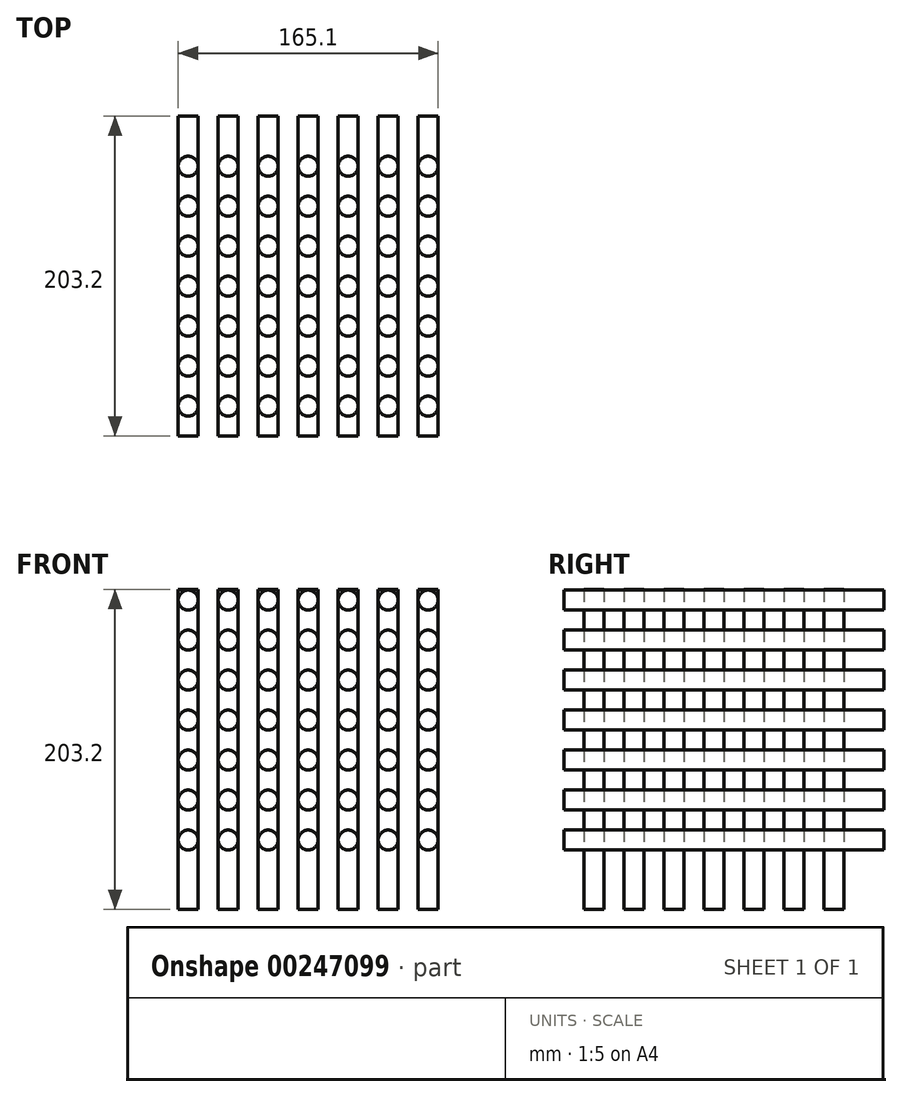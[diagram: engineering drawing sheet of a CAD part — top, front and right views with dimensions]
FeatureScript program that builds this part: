
annotation { "Feature Type Name" : "Feature", "Feature Type Description" : "" }
export const myFeature = defineFeature(function(context is Context, id is Id, definition is map)
    precondition{}
    {
        {
            var Q0;
            Q0=qCreatedBy(makeId("Front.planeOp"),FACE);
            var sketch = newSketch(context, id + "F0", { "sketchPlane" : qUnion([Q0])});
            skCircle(sketch, "E0", {"center": v(-69.84, -57.55) * mm, "radius": 6.35 * mm});
            skCircle(sketch, "E1.0.1.0", {"center": v(-69.84, -32.15) * mm, "radius": 6.35 * mm});
            skCircle(sketch, "E1.0.2.0", {"center": v(-69.84, -6.75) * mm, "radius": 6.35 * mm});
            skCircle(sketch, "E1.0.3.0", {"center": v(-69.84, 18.65) * mm, "radius": 6.35 * mm});
            skCircle(sketch, "E1.0.4.0", {"center": v(-69.84, 44.05) * mm, "radius": 6.35 * mm});
            skCircle(sketch, "E1.0.5.0", {"center": v(-69.84, 69.45) * mm, "radius": 6.35 * mm});
            skCircle(sketch, "E1.0.6.0", {"center": v(-69.84, 94.85) * mm, "radius": 6.35 * mm});
            skCircle(sketch, "E1.1.0.0", {"center": v(-44.44, -57.55) * mm, "radius": 6.35 * mm});
            skCircle(sketch, "E1.1.1.0", {"center": v(-44.44, -32.15) * mm, "radius": 6.35 * mm});
            skCircle(sketch, "E1.1.2.0", {"center": v(-44.44, -6.75) * mm, "radius": 6.35 * mm});
            skCircle(sketch, "E1.1.3.0", {"center": v(-44.44, 18.65) * mm, "radius": 6.35 * mm});
            skCircle(sketch, "E1.1.4.0", {"center": v(-44.44, 44.05) * mm, "radius": 6.35 * mm});
            skCircle(sketch, "E1.1.5.0", {"center": v(-44.44, 69.45) * mm, "radius": 6.35 * mm});
            skCircle(sketch, "E1.1.6.0", {"center": v(-44.44, 94.85) * mm, "radius": 6.35 * mm});
            skCircle(sketch, "E1.2.0.0", {"center": v(-19.04, -57.55) * mm, "radius": 6.35 * mm});
            skCircle(sketch, "E1.2.1.0", {"center": v(-19.04, -32.15) * mm, "radius": 6.35 * mm});
            skCircle(sketch, "E1.2.2.0", {"center": v(-19.04, -6.75) * mm, "radius": 6.35 * mm});
            skCircle(sketch, "E1.2.3.0", {"center": v(-19.04, 18.65) * mm, "radius": 6.35 * mm});
            skCircle(sketch, "E1.2.4.0", {"center": v(-19.04, 44.05) * mm, "radius": 6.35 * mm});
            skCircle(sketch, "E1.2.5.0", {"center": v(-19.04, 69.45) * mm, "radius": 6.35 * mm});
            skCircle(sketch, "E1.2.6.0", {"center": v(-19.04, 94.85) * mm, "radius": 6.35 * mm});
            skCircle(sketch, "E1.3.0.0", {"center": v(6.36, -57.55) * mm, "radius": 6.35 * mm});
            skCircle(sketch, "E1.3.1.0", {"center": v(6.36, -32.15) * mm, "radius": 6.35 * mm});
            skCircle(sketch, "E1.3.2.0", {"center": v(6.36, -6.75) * mm, "radius": 6.35 * mm});
            skCircle(sketch, "E1.3.3.0", {"center": v(6.36, 18.65) * mm, "radius": 6.35 * mm});
            skCircle(sketch, "E1.3.4.0", {"center": v(6.36, 44.05) * mm, "radius": 6.35 * mm});
            skCircle(sketch, "E1.3.5.0", {"center": v(6.36, 69.45) * mm, "radius": 6.35 * mm});
            skCircle(sketch, "E1.3.6.0", {"center": v(6.36, 94.85) * mm, "radius": 6.35 * mm});
            skCircle(sketch, "E1.4.0.0", {"center": v(31.76, -57.55) * mm, "radius": 6.35 * mm});
            skCircle(sketch, "E1.4.1.0", {"center": v(31.76, -32.15) * mm, "radius": 6.35 * mm});
            skCircle(sketch, "E1.4.2.0", {"center": v(31.76, -6.75) * mm, "radius": 6.35 * mm});
            skCircle(sketch, "E1.4.3.0", {"center": v(31.76, 18.65) * mm, "radius": 6.35 * mm});
            skCircle(sketch, "E1.4.4.0", {"center": v(31.76, 44.05) * mm, "radius": 6.35 * mm});
            skCircle(sketch, "E1.4.5.0", {"center": v(31.76, 69.45) * mm, "radius": 6.35 * mm});
            skCircle(sketch, "E1.4.6.0", {"center": v(31.76, 94.85) * mm, "radius": 6.35 * mm});
            skCircle(sketch, "E1.5.0.0", {"center": v(57.16, -57.55) * mm, "radius": 6.35 * mm});
            skCircle(sketch, "E1.5.1.0", {"center": v(57.16, -32.15) * mm, "radius": 6.35 * mm});
            skCircle(sketch, "E1.5.2.0", {"center": v(57.16, -6.75) * mm, "radius": 6.35 * mm});
            skCircle(sketch, "E1.5.3.0", {"center": v(57.16, 18.65) * mm, "radius": 6.35 * mm});
            skCircle(sketch, "E1.5.4.0", {"center": v(57.16, 44.05) * mm, "radius": 6.35 * mm});
            skCircle(sketch, "E1.5.5.0", {"center": v(57.16, 69.45) * mm, "radius": 6.35 * mm});
            skCircle(sketch, "E1.5.6.0", {"center": v(57.16, 94.85) * mm, "radius": 6.35 * mm});
            skCircle(sketch, "E1.6.0.0", {"center": v(82.56, -57.55) * mm, "radius": 6.35 * mm});
            skCircle(sketch, "E1.6.1.0", {"center": v(82.56, -32.15) * mm, "radius": 6.35 * mm});
            skCircle(sketch, "E1.6.2.0", {"center": v(82.56, -6.75) * mm, "radius": 6.35 * mm});
            skCircle(sketch, "E1.6.3.0", {"center": v(82.56, 18.65) * mm, "radius": 6.35 * mm});
            skCircle(sketch, "E1.6.4.0", {"center": v(82.56, 44.05) * mm, "radius": 6.35 * mm});
            skCircle(sketch, "E1.6.5.0", {"center": v(82.56, 69.45) * mm, "radius": 6.35 * mm});
            skCircle(sketch, "E1.6.6.0", {"center": v(82.56, 94.85) * mm, "radius": 6.35 * mm});
            skLineSegment(sketch, "E1.direction1", {"start": v(-69.84, -57.55) * mm, "end": v(-44.44, -57.55) * mm, "construction": true});
            skLineSegment(sketch, "E1.direction2", {"start": v(-69.84, -57.55) * mm, "end": v(-69.84, -32.15) * mm, "construction": true});
            skSolve(sketch);
        }
        {
            var Q0;
            Q0 = qSketchRegion(id + "F0", true);
            extrude(context, id + "F1", {"entities" : qUnion([Q0]), "endBound" : BoundingType.SYMMETRIC, "depth" : 203.2 * mm});
        }
        {
            var Q0;
            Q0=qCreatedBy(makeId("Top.planeOp"),FACE);
            var sketch = newSketch(context, id + "F2", { "sketchPlane" : qUnion([Q0])});
            skCircle(sketch, "E2", {"center": v(-69.84, -82.64) * mm, "radius": 6.35 * mm});
            skCircle(sketch, "E3.0.1.0", {"center": v(-69.84, -57.24) * mm, "radius": 6.35 * mm});
            skCircle(sketch, "E3.0.2.0", {"center": v(-69.84, -31.84) * mm, "radius": 6.35 * mm});
            skCircle(sketch, "E3.0.3.0", {"center": v(-69.84, -6.44) * mm, "radius": 6.35 * mm});
            skCircle(sketch, "E3.0.4.0", {"center": v(-69.84, 18.96) * mm, "radius": 6.35 * mm});
            skCircle(sketch, "E3.0.5.0", {"center": v(-69.84, 44.36) * mm, "radius": 6.35 * mm});
            skCircle(sketch, "E3.0.6.0", {"center": v(-69.84, 69.76) * mm, "radius": 6.35 * mm});
            skCircle(sketch, "E3.1.0.0", {"center": v(-44.44, -82.64) * mm, "radius": 6.35 * mm});
            skCircle(sketch, "E3.1.1.0", {"center": v(-44.44, -57.24) * mm, "radius": 6.35 * mm});
            skCircle(sketch, "E3.1.2.0", {"center": v(-44.44, -31.84) * mm, "radius": 6.35 * mm});
            skCircle(sketch, "E3.1.3.0", {"center": v(-44.44, -6.44) * mm, "radius": 6.35 * mm});
            skCircle(sketch, "E3.1.4.0", {"center": v(-44.44, 18.96) * mm, "radius": 6.35 * mm});
            skCircle(sketch, "E3.1.5.0", {"center": v(-44.44, 44.36) * mm, "radius": 6.35 * mm});
            skCircle(sketch, "E3.1.6.0", {"center": v(-44.44, 69.76) * mm, "radius": 6.35 * mm});
            skCircle(sketch, "E3.2.0.0", {"center": v(-19.04, -82.64) * mm, "radius": 6.35 * mm});
            skCircle(sketch, "E3.2.1.0", {"center": v(-19.04, -57.24) * mm, "radius": 6.35 * mm});
            skCircle(sketch, "E3.2.2.0", {"center": v(-19.04, -31.84) * mm, "radius": 6.35 * mm});
            skCircle(sketch, "E3.2.3.0", {"center": v(-19.04, -6.44) * mm, "radius": 6.35 * mm});
            skCircle(sketch, "E3.2.4.0", {"center": v(-19.04, 18.96) * mm, "radius": 6.35 * mm});
            skCircle(sketch, "E3.2.5.0", {"center": v(-19.04, 44.36) * mm, "radius": 6.35 * mm});
            skCircle(sketch, "E3.2.6.0", {"center": v(-19.04, 69.76) * mm, "radius": 6.35 * mm});
            skCircle(sketch, "E3.3.0.0", {"center": v(6.36, -82.64) * mm, "radius": 6.35 * mm});
            skCircle(sketch, "E3.3.1.0", {"center": v(6.36, -57.24) * mm, "radius": 6.35 * mm});
            skCircle(sketch, "E3.3.2.0", {"center": v(6.36, -31.84) * mm, "radius": 6.35 * mm});
            skCircle(sketch, "E3.3.3.0", {"center": v(6.36, -6.44) * mm, "radius": 6.35 * mm});
            skCircle(sketch, "E3.3.4.0", {"center": v(6.36, 18.96) * mm, "radius": 6.35 * mm});
            skCircle(sketch, "E3.3.5.0", {"center": v(6.36, 44.36) * mm, "radius": 6.35 * mm});
            skCircle(sketch, "E3.3.6.0", {"center": v(6.36, 69.76) * mm, "radius": 6.35 * mm});
            skCircle(sketch, "E3.4.0.0", {"center": v(31.76, -82.64) * mm, "radius": 6.35 * mm});
            skCircle(sketch, "E3.4.1.0", {"center": v(31.76, -57.24) * mm, "radius": 6.35 * mm});
            skCircle(sketch, "E3.4.2.0", {"center": v(31.76, -31.84) * mm, "radius": 6.35 * mm});
            skCircle(sketch, "E3.4.3.0", {"center": v(31.76, -6.44) * mm, "radius": 6.35 * mm});
            skCircle(sketch, "E3.4.4.0", {"center": v(31.76, 18.96) * mm, "radius": 6.35 * mm});
            skCircle(sketch, "E3.4.5.0", {"center": v(31.76, 44.36) * mm, "radius": 6.35 * mm});
            skCircle(sketch, "E3.4.6.0", {"center": v(31.76, 69.76) * mm, "radius": 6.35 * mm});
            skCircle(sketch, "E3.5.0.0", {"center": v(57.16, -82.64) * mm, "radius": 6.35 * mm});
            skCircle(sketch, "E3.5.1.0", {"center": v(57.16, -57.24) * mm, "radius": 6.35 * mm});
            skCircle(sketch, "E3.5.2.0", {"center": v(57.16, -31.84) * mm, "radius": 6.35 * mm});
            skCircle(sketch, "E3.5.3.0", {"center": v(57.16, -6.44) * mm, "radius": 6.35 * mm});
            skCircle(sketch, "E3.5.4.0", {"center": v(57.16, 18.96) * mm, "radius": 6.35 * mm});
            skCircle(sketch, "E3.5.5.0", {"center": v(57.16, 44.36) * mm, "radius": 6.35 * mm});
            skCircle(sketch, "E3.5.6.0", {"center": v(57.16, 69.76) * mm, "radius": 6.35 * mm});
            skCircle(sketch, "E3.6.0.0", {"center": v(82.56, -82.64) * mm, "radius": 6.35 * mm});
            skCircle(sketch, "E3.6.1.0", {"center": v(82.56, -57.24) * mm, "radius": 6.35 * mm});
            skCircle(sketch, "E3.6.2.0", {"center": v(82.56, -31.84) * mm, "radius": 6.35 * mm});
            skCircle(sketch, "E3.6.3.0", {"center": v(82.56, -6.44) * mm, "radius": 6.35 * mm});
            skCircle(sketch, "E3.6.4.0", {"center": v(82.56, 18.96) * mm, "radius": 6.35 * mm});
            skCircle(sketch, "E3.6.5.0", {"center": v(82.56, 44.36) * mm, "radius": 6.35 * mm});
            skCircle(sketch, "E3.6.6.0", {"center": v(82.56, 69.76) * mm, "radius": 6.35 * mm});
            skLineSegment(sketch, "E3.direction1", {"start": v(-69.84, -82.64) * mm, "end": v(-44.44, -82.64) * mm, "construction": true});
            skLineSegment(sketch, "E3.direction2", {"start": v(-69.84, -82.64) * mm, "end": v(-69.84, -57.24) * mm, "construction": true});
            skSolve(sketch);
        }
        {
            var Q0;
            Q0 = qSketchRegion(id + "F2", true);
            extrude(context, id + "F3", {"entities" : qUnion([Q0]), "endBound" : BoundingType.SYMMETRIC, "depth" : 203.2 * mm});
        }
    });
